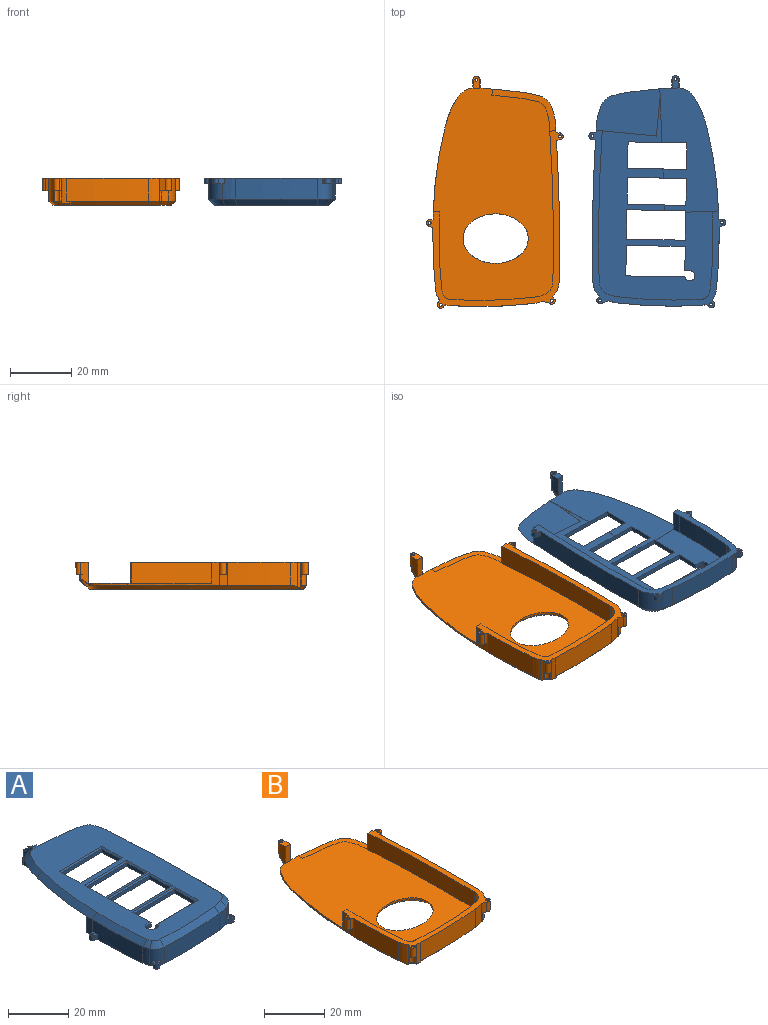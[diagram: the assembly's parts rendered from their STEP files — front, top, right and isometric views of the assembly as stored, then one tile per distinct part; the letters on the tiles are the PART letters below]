
ASSEMBLY  parts=2 mates=1
PART A: 115 faces, bbox 44.6x75.7x9.3 mm
  f0: cylinder r=1.13mm len=2.26mm, axis (0,0,-1), area 7mm2, adj f36,f38,f66,f72
  f1: cylinder r=0.5mm len=1.81mm, axis (0,0,-1), area 5.7mm2, adj f66,f72
  f2: plane 1.81x1.21mm, normal (0,1,0), area 2.2mm2, adj f10,f29,f65,f70
  f3: plane 1.81x0.99mm, normal (-0.41,-0.91,0), area 2mm2, adj f10,f29,f65,f70
  f4: plane 1.83x1.81mm, normal (-0.34,-0.94,0), area 3.5mm2, adj f12,f32,f65,f69
  f5: plane 1.81x0.95mm, normal (0.85,0.52,0), area 2mm2, adj f12,f19,f65,f69
  f6: plane 1.81x0.69mm, normal (0.53,-0.85,0), area 1.5mm2, adj f14,f18,f65,f68
  f7: plane 1.81x0.42mm, normal (-0.87,0.49,0), area 0.9mm2, adj f14,f18,f65,f68
  f8: plane 1.81x0.86mm, normal (0.34,-0.94,0), area 1.7mm2, adj f16,f33,f65,f67
  f9: plane 1.81x0.91mm, normal (0.23,0.97,0), area 1.7mm2, adj f16,f33,f65,f67
  f10: cylinder r=1.08mm len=2.15mm, axis (0,0,-1), area 6mm2, adj f2,f3,f65,f70
  f11: cylinder r=0.5mm len=1.81mm, axis (0,0,-1), area 5.7mm2, adj f65,f70
  f12: cylinder r=1.13mm len=1.9mm, axis (0,0,-1), area 5.7mm2, adj f4,f5,f65,f69
  f13: cylinder r=0.5mm len=1.81mm, axis (0,0,-1), area 5.7mm2, adj f65,f69
  f14: cylinder r=1.13mm len=2.16mm, axis (0,0,-1), area 7.7mm2, adj f6,f7,f65,f68
  f15: cylinder r=0.5mm len=1.81mm, axis (0,0,-1), area 5.7mm2, adj f65,f68
  f16: cylinder r=1.13mm len=2.26mm, axis (0,0,-1), area 7.2mm2, adj f8,f9,f65,f67
  f17: cylinder r=0.5mm len=1.81mm, axis (0,0,-1), area 5.7mm2, adj f65,f67
  f18: cylinder r=4.41mm len=6.71mm, axis (0,0,-1), area 30.1mm2, adj f6,f7,f30,f31,f65,f68,f81
  f19: cylinder r=6.49mm len=6.71mm, axis (0,0,-1), area 49.7mm2, adj f5,f32,f33,f65,f69,f78
  f20: cylinder r=521.44mm len=48.94mm, axis (0,0,-1), area 330.1mm2, adj f28,f35,f40,f65
  f21: cylinder r=127.01mm len=6.71mm, axis (0,0,-1), area 17.9mm2, adj f29,f34,f65,f84
  f22: cylinder r=125.01mm len=6.74mm, axis (0,0,-1), area 17.7mm2, adj f23,f34,f40,f65
  f23: cylinder r=171.29mm len=22.73mm, axis (0,0,-1), area 153.4mm2, adj f22,f24,f40,f65
  f24: cylinder r=6.68mm len=6.74mm, axis (0,0,-1), area 13.2mm2, adj f23,f25,f40,f65
  f25: cylinder r=2.41mm len=6.74mm, axis (0,0,-1), area 19.7mm2, adj f24,f26,f40,f65
  f26: cylinder r=148.75mm len=26.35mm, axis (0,0,-1), area 177.9mm2, adj f25,f27,f40,f65
  f27: cylinder r=18.56mm len=6.74mm, axis (0,0,-1), area 27mm2, adj f26,f28,f40,f65
  f28: cylinder r=4.49mm len=6.74mm, axis (0,0,-1), area 38.3mm2, adj f20,f27,f40,f65
  f29: cylinder r=173.29mm len=23.03mm, axis (0,0,-1), area 150.1mm2, adj f2,f3,f21,f30,f65,f70,f83
  f30: cylinder r=8.68mm len=6.71mm, axis (0,0,-1), area 17.2mm2, adj f18,f29,f65,f82
  f31: cylinder r=150.75mm len=26.6mm, axis (0,0,-1), area 178.7mm2, adj f18,f32,f65,f80
  f32: cylinder r=20.56mm len=6.71mm, axis (0,0,-1), area 28.6mm2, adj f4,f19,f31,f65,f69,f79
  f33: cylinder r=523.44mm len=49.13mm, axis (0,0,-1), area 324.8mm2, adj f8,f9,f19,f35,f65,f67,f77
  f34: plane 10.72x6.78mm, normal (0.04,1,0), area 13.9mm2, adj f21,f22,f39,f40,f50,f65,f84
  f35: plane 19.64x6.77mm, normal (-0.09,1,0), area 14mm2, adj f20,f33,f40,f63,f64,f65,f77
  f36: plane 7.54x3.31mm, normal (-1,0,0), area 15.9mm2, adj f0,f37,f39,f66,f71,f86,f105,f108
  f37: plane 6.78x2.23mm, normal (-0.09,-1,0), area 15.1mm2, adj f36,f38,f39,f66
  f38: plane 7.8x3.88mm, normal (1,0,0), area 18.7mm2, adj f0,f37,f39,f66,f71,f73,f109,f112
  f39: plane 40.52x19.11mm, normal (0,0,-1), area 482.8mm2, adj f34,f36,f37,f38,f49,f50,f51,f53
  f40: plane 66.24x37.28mm, normal (0,0,-1), area 988.9mm2, adj f20,f22,f23,f24,f25,f26,f27,f28
  f41: plane 7.88x1.49mm, normal (1,0.02,0), area 11.8mm2, adj f40,f42,f46,f102
  f42: plane 1.66x1.49mm, normal (0.03,-1,0), area 2.5mm2, adj f40,f41,f43,f100
  f43: cylinder r=1.64mm len=3.27mm, axis (0,0,1), area 10.9mm2, adj f40,f42,f44,f99
  f44: plane 19.23x1.49mm, normal (-0.02,1,0), area 28.7mm2, adj f40,f43,f45,f101
  f45: plane 9.92x1.49mm, normal (-1,-0.02,0), area 14.8mm2, adj f40,f44,f46,f103
  f46: plane 19.19x1.49mm, normal (0.02,-1,0), area 28.6mm2, adj f40,f41,f45,f104
  f47: plane 19.19x1.49mm, normal (-0.02,1,0), area 28.6mm2, adj f40,f48,f50,f95
  f48: plane 9.58x1.49mm, normal (-1,-0.02,0), area 14.3mm2, adj f40,f47,f49,f97
  f49: plane 19.19x1.49mm, normal (0.02,-1,0), area 28.4mm2, adj f39,f40,f48,f50,f60,f98
  f50: plane 9.58x1.49mm, normal (1,0.02,0), area 14.3mm2, adj f34,f39,f40,f47,f49,f96
  f51: plane 19.19x1.49mm, normal (-0.02,1,0), area 28.4mm2, adj f39,f40,f52,f54,f60,f91
  f52: plane 8.77x1.49mm, normal (-1,-0.02,0), area 13.1mm2, adj f40,f51,f53,f93
  f53: plane 19.19x1.49mm, normal (0.02,-1,0), area 28.4mm2, adj f39,f40,f52,f54,f61,f94
  f54: plane 8.76x1.46mm, normal (1,0.02,0), area 12.7mm2, adj f39,f51,f53,f92
  f55: plane 19.19x1.49mm, normal (-0.02,1,0), area 28.3mm2, adj f39,f40,f56,f58,f61,f87
  f56: plane 8.63x1.49mm, normal (-1,-0.02,0), area 12.9mm2, adj f40,f55,f57,f88
  f57: plane 19.19x1.49mm, normal (0.02,-1,0), area 28.3mm2, adj f39,f40,f56,f58,f62,f90
  f58: plane 8.64x1.46mm, normal (1,0.02,0), area 12.6mm2, adj f39,f55,f57,f89
  f59: plane 67.1x37.22mm, normal (0,0,1), area 1449.3mm2, adj f73,f74,f75,f76,f77,f78,f79,f80
  f60: plane 1.76x0.07mm, normal (-1,0.04,0), area 0.1mm2, adj f39,f40,f49,f51
  f61: plane 2.96x0.11mm, normal (-1,0.04,0), area 0.1mm2, adj f39,f40,f53,f55
  f62: plane 17.45x0.67mm, normal (-1,0.04,0), area 0.6mm2, adj f39,f40,f57,f63,f64,f73
  f63: plane 20.8x15.36mm, normal (0,0,-1), area 255.1mm2, adj f35,f62,f64,f73,f74,f75,f76,f77
  f64: plane 12.82x1.22mm, normal (0.99,0.09,-0.12), area 0.3mm2, adj f35,f40,f62,f63
  f65: plane 57.86x44.54mm, normal (0,0,-1), area 251.8mm2, adj f2,f3,f4,f5,f6,f7,f8,f9
  f66: plane 4.15x2.26mm, normal (0,0,-1), area 7.7mm2, adj f0,f1,f36,f37,f38
  f67: plane 2.75x2.32mm, normal (0,0,1), area 3.9mm2, adj f8,f9,f16,f17,f33
  f68: plane 2.84x2.54mm, normal (0,0,1), area 3.1mm2, adj f6,f7,f14,f15,f18
  f69: plane 3.72x2.61mm, normal (0,0,1), area 4mm2, adj f4,f5,f12,f13,f19,f32
  f70: plane 2.58x2.18mm, normal (0,0,1), area 3.6mm2, adj f2,f3,f10,f11,f29
  f71: cylinder r=1.13mm len=4.11mm, axis (0,0,1), area 13.2mm2, adj f36,f38,f72,f114
  f72: plane 2.26x2.26mm, normal (0,0,1), area 3.2mm2, adj f0,f1,f71
  f73: cone r=125.61mm half-angle=45deg, axis (0,0,-1), area 30.8mm2, adj f38,f39,f59,f62,f63,f74,f107,f112
  f74: cone r=37.91mm half-angle=45deg, axis (0,0,-1), area 22.1mm2, adj f59,f63,f73,f75
  f75: cone r=4.01mm half-angle=45deg, axis (0,0,-1), area 15.2mm2, adj f59,f63,f74,f76
  f76: cone r=17.49mm half-angle=45deg, axis (0,0,-1), area 19.6mm2, adj f59,f63,f75,f77
  f77: cone r=521.41mm half-angle=45deg, axis (0,0,-1), area 141.3mm2, adj f33,f35,f59,f63,f76,f78
  f78: cone r=4.46mm half-angle=45deg, axis (0,0,-1), area 19.9mm2, adj f19,f59,f77,f79
  f79: cone r=18.53mm half-angle=45deg, axis (0,0,-1), area 12.1mm2, adj f32,f59,f78,f80
  f80: cone r=148.72mm half-angle=45deg, axis (0,0,-1), area 76.2mm2, adj f31,f59,f79,f81
  f81: cone r=2.38mm half-angle=45deg, axis (0,0,-1), area 11.6mm2, adj f18,f59,f80,f82
  f82: cone r=6.65mm half-angle=45deg, axis (0,0,-1), area 6.5mm2, adj f30,f59,f81,f83
  f83: cone r=171.25mm half-angle=45deg, axis (0,0,-1), area 65.8mm2, adj f29,f59,f82,f84
  f84: cone r=124.98mm half-angle=45deg, axis (0,0,-1), area 83.3mm2, adj f21,f34,f39,f59,f83,f85
  f85: cone r=27.73mm half-angle=45deg, axis (0,0,-1), area 29.4mm2, adj f39,f59,f84,f86
  f86: cone r=4.69mm half-angle=45deg, axis (0,0,-1), area 13.6mm2, adj f36,f39,f59,f85,f105,f106,f110
  f87: plane 20.2x0.85mm, normal (-0.01,0.71,0.71), area 14.2mm2, adj f55,f59,f88,f89
  f88: plane 9.64x0.66mm, normal (-0.71,-0.01,0.71), area 6.6mm2, adj f56,f59,f87,f90
  f89: plane 9.66x0.66mm, normal (0.71,0.01,0.71), area 6.6mm2, adj f58,f59,f87,f90
  f90: plane 20.2x0.84mm, normal (0.01,-0.71,0.71), area 14.2mm2, adj f57,f59,f88,f89
  f91: plane 20.2x0.84mm, normal (-0.01,0.71,0.71), area 14.2mm2, adj f51,f59,f92,f93
  f92: plane 9.77x0.66mm, normal (0.71,0.01,0.71), area 6.7mm2, adj f54,f59,f91,f94
  f93: plane 9.79x0.66mm, normal (-0.71,-0.01,0.71), area 6.7mm2, adj f52,f59,f91,f94
  f94: plane 20.2x0.85mm, normal (0.01,-0.71,0.71), area 14.2mm2, adj f53,f59,f92,f93
  f95: plane 20.2x0.84mm, normal (-0.01,0.71,0.71), area 14.2mm2, adj f47,f59,f96,f97
  f96: plane 10.6x0.68mm, normal (0.71,0.01,0.71), area 7.3mm2, adj f50,f59,f95,f98
  f97: plane 10.6x0.68mm, normal (-0.71,-0.01,0.71), area 7.3mm2, adj f48,f59,f95,f98
  f98: plane 20.2x0.84mm, normal (0.01,-0.71,0.71), area 14.2mm2, adj f49,f59,f96,f97
  f99: cone r=1.64mm half-angle=45deg, axis (0,0,1), area 5.9mm2, adj f43,f59,f100,f101
  f100: plane 1.67x0.54mm, normal (0.02,-0.71,0.71), area 1mm2, adj f42,f59,f99,f102
  f101: plane 19.79x0.86mm, normal (-0.01,0.71,0.71), area 13.9mm2, adj f44,f59,f99,f103
  f102: plane 8.38x0.65mm, normal (0.71,0.01,0.71), area 5.7mm2, adj f41,f59,f100,f104
  f103: plane 10.94x0.68mm, normal (-0.71,-0.01,0.71), area 7.5mm2, adj f45,f59,f101,f104
  f104: plane 20.2x0.84mm, normal (0.01,-0.71,0.71), area 14.2mm2, adj f46,f59,f102,f103
  f105: cone r=5.14mm half-angle=53.8deg, axis (0,0,1), area 0.3mm2, adj f36,f86,f106,f108
  f106: bspline ~4.58x3.28mm, area 3.5mm2, adj f86,f105,f108,f110,f111,f113,f114
  f107: bspline ~4.97x3.44mm, area 3.7mm2, adj f73,f109,f111,f112,f113,f114
  f108: cone r=1.13mm half-angle=36.2deg, axis (0,0,-1), area 0mm2, adj f36,f105,f106
  f109: cone r=1.13mm half-angle=36.2deg, axis (0,0,-1), area 0.1mm2, adj f38,f107,f112
  f110: bspline ~0.78x0.63mm, area 0mm2, adj f86,f106,f113
  f111: cone r=4.69mm half-angle=53.8deg, axis (0,0,1), area 9.9mm2, adj f106,f107,f113,f114
  f112: cone r=5.14mm half-angle=53.8deg, axis (0,0,1), area 0.3mm2, adj f38,f73,f107,f109
  f113: cone r=4.99mm half-angle=81.2deg, axis (0,0,-1), area 1.6mm2, adj f59,f106,f107,f110,f111
  f114: cone r=1.13mm half-angle=8.8deg, axis (0,0,1), area 1.9mm2, adj f71,f106,f107,f111
PART B: 95 faces, bbox 44.6x75.7x9.2 mm
  f0: plane 0.09x0.04mm, normal (1,0,0), area 0mm2, adj f16,f78,f90
  f1: plane 0.01x0mm, normal (-1,0,0), area 0mm2, adj f16,f83,f91
  f2: cylinder r=0.5mm len=4.04mm, axis (0,0,-1), area 12.7mm2, adj f54,f58
  f3: cylinder r=0.5mm len=4.04mm, axis (0,0,-1), area 12.7mm2, adj f54,f61
  f4: cylinder r=0.5mm len=4.04mm, axis (0,0,-1), area 12.7mm2, adj f55,f66
  f5: cylinder r=0.5mm len=4.04mm, axis (0,0,-1), area 12.7mm2, adj f54,f62
  f6: cylinder r=1.13mm len=4.04mm, axis (0,0,-1), area 12.8mm2, adj f7,f8,f54,f62
  f7: plane 4.04x0.95mm, normal (0.85,0.52,0), area 4.5mm2, adj f6,f49,f54,f62
  f8: plane 7.47x1.83mm, normal (-0.34,-0.94,0), area 7.9mm2, adj f6,f31,f54,f62,f64,f69
  f9: cylinder r=1.08mm len=4.04mm, axis (0,0,-1), area 13.5mm2, adj f10,f11,f54,f61
  f10: plane 7.47x0.99mm, normal (-0.41,-0.91,0), area 4.4mm2, adj f9,f42,f54,f60,f61,f76
  f11: plane 7.5x1.21mm, normal (0,1,0), area 5mm2, adj f9,f43,f54,f60,f61,f77
  f12: cylinder r=1.13mm len=4.04mm, axis (0,0,-1), area 16.1mm2, adj f13,f45,f54,f57
  f13: plane 4.04x0.91mm, normal (0.23,0.97,0), area 3.8mm2, adj f12,f14,f54,f57
  f14: cylinder r=523.44mm len=4.04mm, axis (0,0,-1), area 2.3mm2, adj f13,f47,f54,f57
  f15: cylinder r=1.13mm len=4.04mm, axis (0,0,-1), area 17.2mm2, adj f50,f51,f54,f58
  f16: plane 69.78x38.85mm, normal (0,0,-1), area 2084.6mm2, adj f0,f1,f45,f67,f68,f69,f70,f71
  f17: cylinder r=0.5mm len=4.04mm, axis (0,0,-1), area 12.7mm2, adj f54,f57
  f18: extruded ~21.25x16.14mm, area 43.1mm2, adj f26,f86
  f19: cylinder r=6.05mm len=4.5mm, axis (0,0,-1), area 4.7mm2, adj f20,f22,f23,f80
  f20: cylinder r=39.94mm len=7.92mm, axis (0,0,-1), area 5.8mm2, adj f19,f23,f25,f79
  f21: cylinder r=29.76mm len=10.06mm, axis (0,0,-1), area 8mm2, adj f24,f26,f44,f77,f84
  f22: cylinder r=19.52mm len=7.18mm, axis (0,0,-1), area 5.3mm2, adj f19,f23,f56,f81
  f23: plane 20.84x13.75mm, normal (0,0,1), area 55.2mm2, adj f19,f20,f22,f25,f26,f47,f56
  f24: cylinder r=6.72mm len=4.96mm, axis (0,0,-1), area 4.3mm2, adj f21,f26,f30,f83,f88,f91
  f25: cylinder r=127.64mm len=11.11mm, axis (0,0,-1), area 8.1mm2, adj f20,f23,f26,f28,f78,f87,f89
  f26: plane 69.21x39.16mm, normal (0,0,1), area 2124.5mm2, adj f18,f21,f23,f24,f25,f28,f29,f30
  f27: cylinder r=1.13mm len=4.04mm, axis (0,0,-1), area 15.7mm2, adj f28,f30,f55,f66
  f28: plane 7.37x3.09mm, normal (1,0,0), area 18.4mm2, adj f25,f26,f27,f29,f55,f65,f87,f93
  f29: plane 6.74x2.23mm, normal (-0.09,-1,0), area 15.1mm2, adj f26,f28,f30,f55
  f30: plane 7.23x2.59mm, normal (-1,0,0), area 15.7mm2, adj f24,f26,f27,f29,f55,f65,f88,f92
  f31: cylinder r=20.56mm len=7.47mm, axis (0,0,-1), area 28.4mm2, adj f8,f32,f54,f68
  f32: cylinder r=150.75mm len=26.6mm, axis (0,0,-1), area 199mm2, adj f31,f53,f54,f67
  f33: plane 6.74x2mm, normal (0.04,1,0), area 13.5mm2, adj f26,f40,f44,f54
  f34: cylinder r=4.49mm len=6.74mm, axis (0,0,-1), area 38.3mm2, adj f26,f35,f48,f54
  f35: cylinder r=18.56mm len=6.74mm, axis (0,0,-1), area 27mm2, adj f26,f34,f36,f54
  f36: cylinder r=148.75mm len=26.35mm, axis (0,0,-1), area 177.9mm2, adj f26,f35,f37,f54
  f37: cylinder r=2.41mm len=6.74mm, axis (0,0,-1), area 19.7mm2, adj f26,f36,f38,f54
  f38: cylinder r=6.68mm len=6.74mm, axis (0,0,-1), area 13.2mm2, adj f26,f37,f39,f54
  f39: cylinder r=171.29mm len=22.73mm, axis (0,0,-1), area 153.4mm2, adj f26,f38,f40,f54
  f40: cylinder r=125.01mm len=6.74mm, axis (0,0,-1), area 17.7mm2, adj f26,f33,f39,f54
  f41: cylinder r=8.68mm len=7.95mm, axis (0,0,-1), area 19.7mm2, adj f42,f52,f54,f75
  f42: cylinder r=173.29mm len=20.41mm, axis (0,0,-1), area 152.7mm2, adj f10,f41,f54,f75
  f43: cylinder r=173.29mm len=7.5mm, axis (0,0,-1), area 0.3mm2, adj f11,f44,f54,f77
  f44: cylinder r=127.01mm len=29.82mm, axis (0,0,-1), area 40.2mm2, adj f21,f26,f33,f43,f54,f77
  f45: plane 8.74x2.11mm, normal (0.34,-0.94,0), area 3.7mm2, adj f12,f16,f46,f54,f56,f57,f73,f82
  f46: cylinder r=523.44mm len=45.81mm, axis (0,0,-1), area 342.4mm2, adj f45,f49,f54,f73
  f47: plane 6.75x1.99mm, normal (-0.09,1,0), area 13.5mm2, adj f14,f23,f48,f54,f56,f57
  f48: cylinder r=521.44mm len=48.94mm, axis (0,0,-1), area 330.1mm2, adj f26,f34,f47,f54
  f49: cylinder r=6.49mm len=7.47mm, axis (0,0,-1), area 40mm2, adj f7,f46,f54,f63,f72
  f50: plane 7.78x0.42mm, normal (-0.87,0.49,0), area 3.7mm2, adj f15,f52,f54,f59,f74
  f51: plane 8.05x0.69mm, normal (0.53,-0.85,0), area 6.3mm2, adj f15,f53,f54,f59,f74
  f52: cylinder r=4.41mm len=8.19mm, axis (0,0,-1), area 8.6mm2, adj f41,f50,f54,f74,f75
  f53: cylinder r=4.41mm len=8.06mm, axis (0,0,-1), area 13.3mm2, adj f32,f51,f54,f67,f74,f85
  f54: plane 57.86x44.54mm, normal (0,0,1), area 251.8mm2, adj f2,f3,f5,f6,f7,f8,f9,f10
  f55: plane 4.15x2.26mm, normal (0,0,1), area 7.7mm2, adj f4,f27,f28,f29,f30
  f56: cylinder r=553.96mm len=3.43mm, axis (0,0,-1), area 11.4mm2, adj f22,f23,f45,f47,f57,f82
  f57: plane 3.32x2.36mm, normal (0,0,-1), area 3.9mm2, adj f12,f13,f14,f17,f45,f47,f56
  f58: plane 2.26x2.26mm, normal (0,0,-1), area 3.2mm2, adj f2,f15,f59
  f59: cylinder r=1.13mm len=3.43mm, axis (0,0,-1), area 9.8mm2, adj f50,f51,f58,f74
  f60: cylinder r=147.44mm len=3.43mm, axis (0,0,-1), area 8.8mm2, adj f10,f11,f61,f77
  f61: plane 2.58x2.16mm, normal (0,0,-1), area 3.5mm2, adj f3,f9,f10,f11,f60
  f62: plane 3.71x2.61mm, normal (0,0,-1), area 4mm2, adj f5,f6,f7,f8,f63,f64
  f63: cylinder r=6.48mm len=3.43mm, axis (0,0,-1), area 9.6mm2, adj f49,f62,f64,f71
  f64: cylinder r=19.49mm len=3.43mm, axis (0,0,-1), area 2.3mm2, adj f8,f62,f63,f70
  f65: cylinder r=1.13mm len=2.37mm, axis (0,0,-1), area 7.2mm2, adj f28,f30,f66,f89,f91,f94
  f66: plane 2.26x2.26mm, normal (0,0,-1), area 3.2mm2, adj f4,f27,f65
  f67: cone r=150.75mm half-angle=45deg, axis (0,0,1), area 45.2mm2, adj f16,f32,f53,f68,f85
  f68: cone r=20.56mm half-angle=45deg, axis (0,0,1), area 7mm2, adj f16,f31,f67,f69
  f69: plane 1.35x1.28mm, normal (-0.24,-0.67,-0.71), area 0mm2, adj f8,f16,f68,f70
  f70: cone r=18.22mm half-angle=45deg, axis (0,0,1), area 0.8mm2, adj f16,f64,f69,f71
  f71: cone r=5.21mm half-angle=45deg, axis (0,0,1), area 4.5mm2, adj f16,f63,f70,f72
  f72: cone r=6.49mm half-angle=45deg, axis (0,0,1), area 8.7mm2, adj f16,f49,f71,f73
  f73: cone r=523.44mm half-angle=45deg, axis (0,0,1), area 81.9mm2, adj f16,f45,f46,f72
  f74: cone r=2.4mm half-angle=45deg, axis (0,0,-1), area 5.7mm2, adj f16,f50,f51,f52,f53,f59,f75,f85
  f75: cone r=173.29mm half-angle=45deg, axis (0,0,1), area 41.3mm2, adj f16,f41,f42,f52,f74,f76
  f76: plane 1.3x1.27mm, normal (-0.29,-0.65,-0.71), area 0mm2, adj f10,f16,f75,f77
  f77: cone r=146.17mm half-angle=45deg, axis (0,0,1), area 64.4mm2, adj f11,f16,f21,f43,f44,f60,f76,f84
  f78: cone r=127.64mm half-angle=45deg, axis (0,0,1), area 19.9mm2, adj f0,f16,f25,f79,f89,f90
  f79: cone r=39.94mm half-angle=45deg, axis (0,0,1), area 14.3mm2, adj f16,f20,f78,f80
  f80: cone r=6.05mm half-angle=45deg, axis (0,0,1), area 10.5mm2, adj f16,f19,f79,f81
  f81: cone r=19.52mm half-angle=45deg, axis (0,0,1), area 12.8mm2, adj f16,f22,f80,f82
  f82: cone r=553.96mm half-angle=45deg, axis (0,0,-1), area 6.4mm2, adj f16,f45,f56,f81
  f83: cone r=6.72mm half-angle=45deg, axis (0,0,1), area 9.6mm2, adj f1,f16,f24,f84,f91
  f84: cone r=29.76mm half-angle=45deg, axis (0,0,1), area 15.9mm2, adj f16,f21,f77,f83
  f85: cone r=4.41mm half-angle=45deg, axis (0,0,1), area 3mm2, adj f16,f53,f67,f74
  f86: bspline ~23.79x18.68mm, area 113.1mm2, adj f16,f18
  f87: cone r=4.36mm half-angle=45deg, axis (0,0,-1), area 0.4mm2, adj f25,f28,f89,f93
  f88: cone r=4.36mm half-angle=45deg, axis (0,0,-1), area 0.3mm2, adj f24,f30,f91,f92
  f89: bspline ~4.16x3.59mm, area 3.1mm2, adj f16,f25,f65,f78,f87,f90,f93,f94
  f90: cone r=4.18mm half-angle=45deg, axis (0,0,1), area 0mm2, adj f0,f78,f89
  f91: bspline ~4.02x3.59mm, area 2.9mm2, adj f1,f16,f24,f65,f83,f88,f92,f94
  f92: cone r=1.13mm half-angle=45deg, axis (0,0,1), area 0.1mm2, adj f30,f88,f91
  f93: cone r=1.13mm half-angle=45deg, axis (0,0,1), area 0.1mm2, adj f28,f87,f89
  f94: cone r=3.82mm half-angle=45deg, axis (0,0,-1), area 7.9mm2, adj f16,f65,f89,f91
PLACE A rot(axis=(0,1,0),180deg) t=(115.32,-71.38,17.5)mm
PLACE B t=(-64.2,-71.51,0)mm
MATE fastened A.f59 <-> B.f16  axis (0,0,-1) through (50.8,0,0)mm
